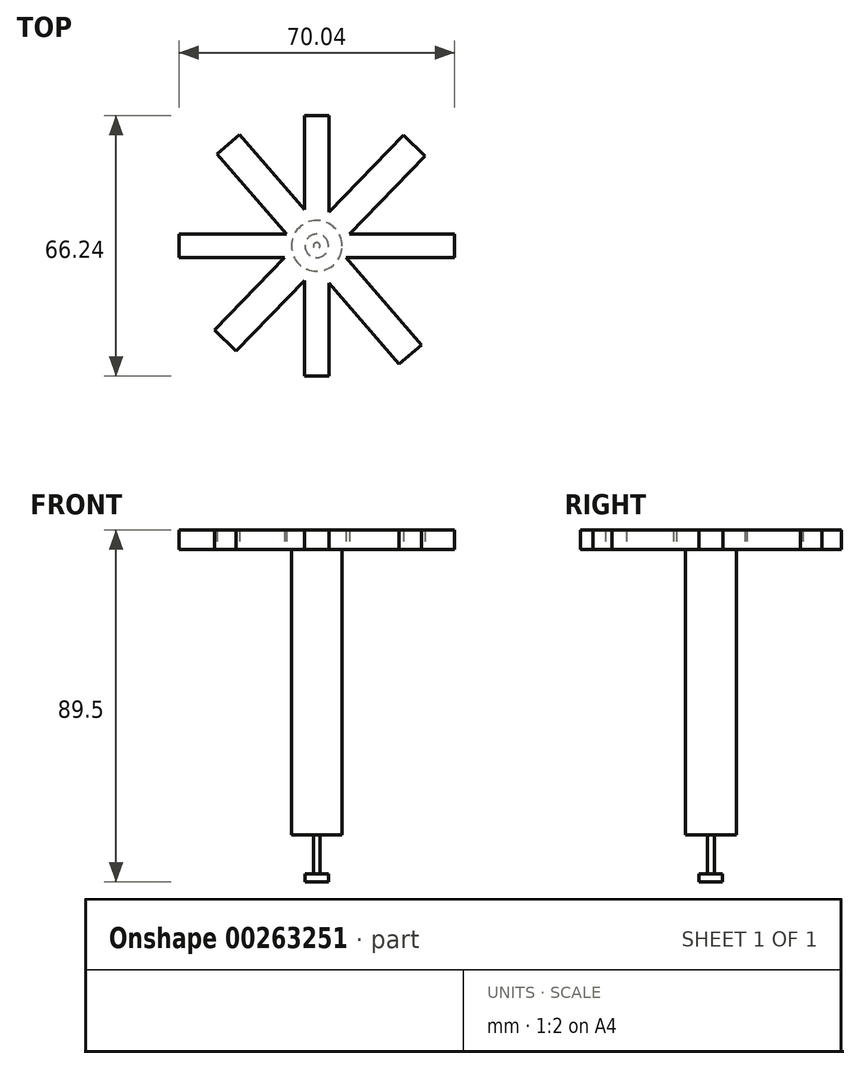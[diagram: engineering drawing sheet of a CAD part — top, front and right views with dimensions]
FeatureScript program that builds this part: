
annotation { "Feature Type Name" : "Feature", "Feature Type Description" : "" }
export const myFeature = defineFeature(function(context is Context, id is Id, definition is map)
    precondition{}
    {
        {
            var Q0;
            Q0=qCreatedBy(makeId("Top.planeOp"),FACE);
            var sketch = newSketch(context, id + "F0", { "sketchPlane" : qUnion([Q0])});
            skCircle(sketch, "E0", {"center": v(0, 0) * mm, "radius": 6.45 * mm});
            skSolve(sketch);
        }
        {
            var Q0;
            Q0 = qSketchRegion(id + "F0", true);
            extrude(context, id + "F1", {"entities" : qUnion([Q0]), "depth" : 75 * mm});
        }
        {
            var Q0;
            Q0=makeQuery(id+"F1.opExtrude","CAP_FACE",FACE,{"disambiguationData":[OSD([sQuery(id+"F0.wireOp",EDGE,"E0")])],"isStart":false});
            var sketch = newSketch(context, id + "F2", { "sketchPlane" : qUnion([Q0])});
            skLineSegment(sketch, "E1.bottom", {"start": v(35.02, -3.01) * mm, "end": v(7.44, -3.01) * mm});
            skLineSegment(sketch, "E1.top", {"start": v(35.02, 3.01) * mm, "end": v(8.35, 3.01) * mm});
            skLineSegment(sketch, "E1.left", {"start": v(35.02, -3.01) * mm, "end": v(35.02, 3.01) * mm});
            skLineSegment(sketch, "E1.right", {"start": v(-35.02, -3.01) * mm, "end": v(-35.02, 3.01) * mm});
            skPoint(sketch, "E1.middle", {"position": v(0, 0) * mm});
            skLineSegment(sketch, "E2.bottom", {"start": v(3.11, -33.12) * mm, "end": v(-3.11, -33.12) * mm});
            skLineSegment(sketch, "E2.top", {"start": v(3.11, 33.12) * mm, "end": v(-3.11, 33.12) * mm});
            skLineSegment(sketch, "E2.left", {"start": v(3.11, -33.12) * mm, "end": v(3.11, -9.48) * mm});
            skLineSegment(sketch, "E2.right", {"start": v(-3.11, -33.12) * mm, "end": v(-3.11, -8.82) * mm});
            skLineSegment(sketch, "E3", {"start": v(-26.02, -21.42) * mm, "end": v(-8.19, -3.01) * mm});
            skLineSegment(sketch, "E4", {"start": v(-26.02, -21.42) * mm, "end": v(-20.5, -26.77) * mm});
            skLineSegment(sketch, "E5", {"start": v(-20.5, -26.77) * mm, "end": v(-3.11, -8.82) * mm});
            skLineSegment(sketch, "E6", {"start": v(27.48, 22.76) * mm, "end": v(22.04, 28.19) * mm});
            skLineSegment(sketch, "E7", {"start": v(-19.67, 28.28) * mm, "end": v(-3.11, 9.17) * mm});
            skLineSegment(sketch, "E8", {"start": v(-19.67, 28.28) * mm, "end": v(-25.34, 23.36) * mm});
            skLineSegment(sketch, "E9", {"start": v(-25.34, 23.36) * mm, "end": v(-7.71, 3.01) * mm});
            skLineSegment(sketch, "E10", {"start": v(20.89, -30) * mm, "end": v(26.63, -25.17) * mm});
            skLineSegment(sketch, "E11.trimOffspring", {"start": v(-3.11, 9.17) * mm, "end": v(-3.11, 33.12) * mm});
            skLineSegment(sketch, "E12.trimOffspring", {"start": v(-7.71, 3.01) * mm, "end": v(-35.02, 3.01) * mm});
            skLineSegment(sketch, "E13.trimOffspring", {"start": v(7.44, -3.01) * mm, "end": v(26.63, -25.17) * mm});
            skLineSegment(sketch, "E14.trimOffspring", {"start": v(3.11, 8.65) * mm, "end": v(22.04, 28.19) * mm});
            skLineSegment(sketch, "E15.trimOffspring", {"start": v(3.11, 8.65) * mm, "end": v(3.11, 33.12) * mm});
            skLineSegment(sketch, "E16.trimOffspring", {"start": v(8.35, 3.01) * mm, "end": v(27.48, 22.76) * mm});
            skLineSegment(sketch, "E17.trimOffspring", {"start": v(3.11, -9.48) * mm, "end": v(20.89, -30) * mm});
            skLineSegment(sketch, "E18.trimOffspring", {"start": v(-8.19, -3.01) * mm, "end": v(-35.02, -3.01) * mm});
            skSolve(sketch);
        }
        {
            var Q0;
            Q0 = qSketchRegion(id + "F2", true);
            extrude(context, id + "F3", {"entities" : qUnion([Q0]), "operationType" : NewBodyOperationType.ADD, "endBound" : BoundingType.SYMMETRIC, "depth" : 5 * mm});
        }
        {
            var Q0;
            Q0=makeQuery(id+"F1.opExtrude","CAP_FACE",FACE,{"disambiguationData":[OSD([sQuery(id+"F0.wireOp",EDGE,"E0")])],"isStart":true});
            var sketch = newSketch(context, id + "F4", { "sketchPlane" : qUnion([Q0])});
            skCircle(sketch, "E19", {"center": v(0, 0) * mm, "radius": 0.83 * mm});
            skSolve(sketch);
        }
        {
            var Q0;
            Q0 = qSketchRegion(id + "F4", true);
            extrude(context, id + "F5", {"entities" : qUnion([Q0]), "operationType" : NewBodyOperationType.ADD, "depth" : 10 * mm});
        }
        {
            var Q0;
            Q0=makeQuery(id+"F5.opExtrude","CAP_FACE",FACE,{"disambiguationData":[OSD([sQuery(id+"F4.wireOp",EDGE,"E19")])],"isStart":false});
            var sketch = newSketch(context, id + "F6", { "sketchPlane" : qUnion([Q0])});
            skCircle(sketch, "E20", {"center": v(0, 0) * mm, "radius": 2.99 * mm});
            skSolve(sketch);
        }
        {
            var Q0;
            Q0 = qSketchRegion(id + "F6", true);
            extrude(context, id + "F7", {"entities" : qUnion([Q0]), "operationType" : NewBodyOperationType.ADD, "depth" : 2 * mm});
        }
    });
